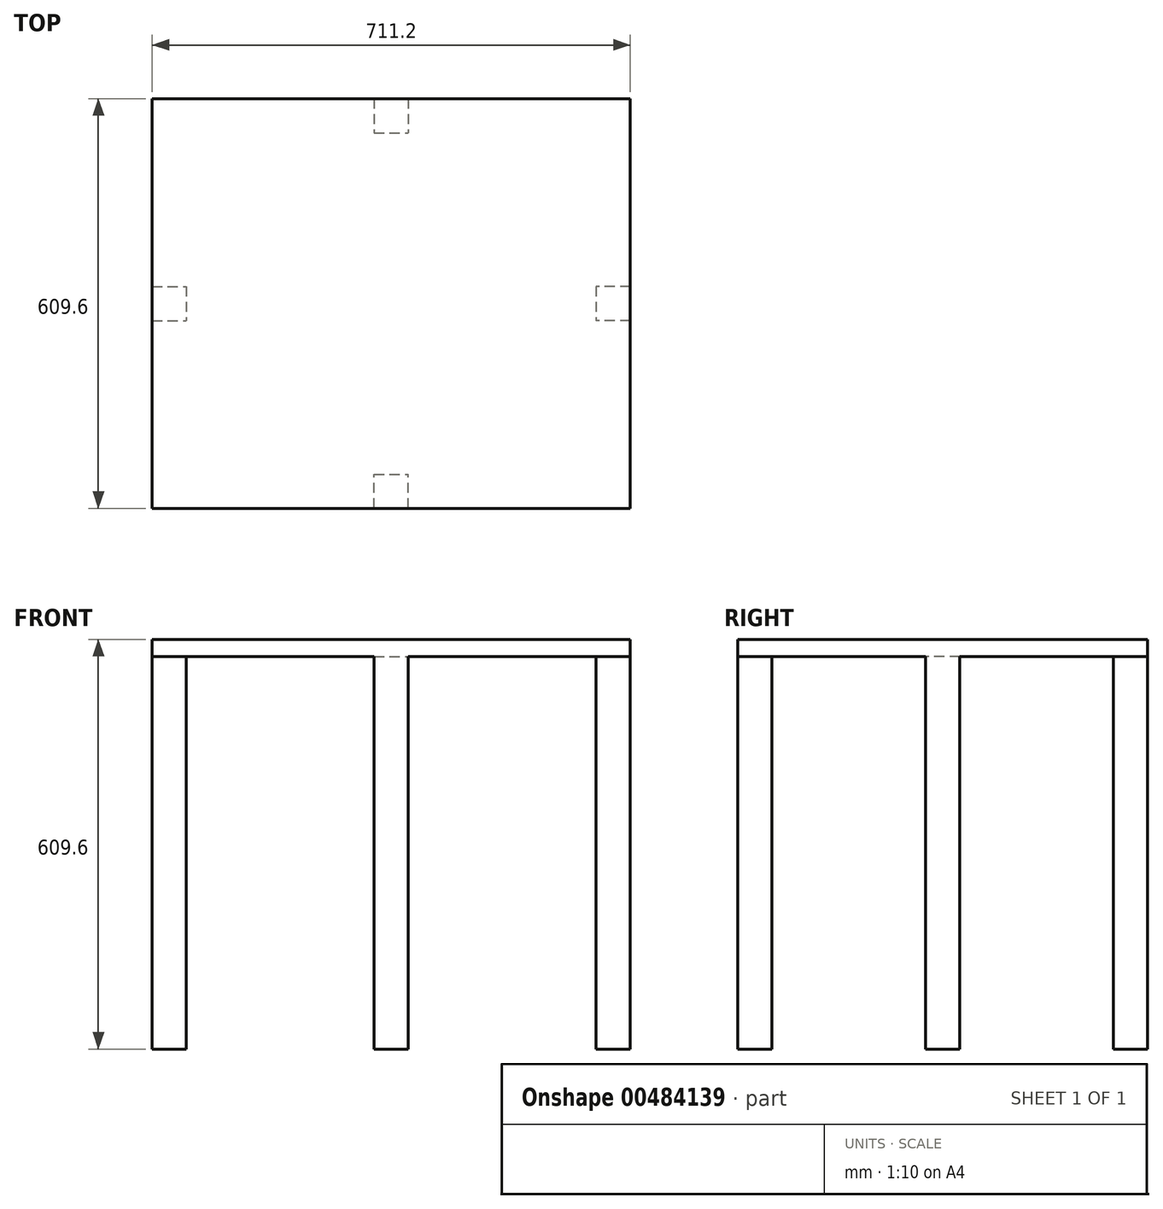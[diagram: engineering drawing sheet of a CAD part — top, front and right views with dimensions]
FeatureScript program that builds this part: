
annotation { "Feature Type Name" : "Feature", "Feature Type Description" : "" }
export const myFeature = defineFeature(function(context is Context, id is Id, definition is map)
    precondition{}
    {
        {
            var Q0;
            Q0=qCreatedBy(makeId("Top.planeOp"),FACE);
            var sketch = newSketch(context, id + "F0", { "sketchPlane" : qUnion([Q0])});
            skLineSegment(sketch, "E0.bottom", {"start": v(0, 0) * mm, "end": v(711.2, 0) * mm});
            skLineSegment(sketch, "E0.top", {"start": v(0, 609.6) * mm, "end": v(711.2, 609.6) * mm});
            skLineSegment(sketch, "E0.left", {"start": v(0, 0) * mm, "end": v(0, 609.6) * mm});
            skLineSegment(sketch, "E0.right", {"start": v(711.2, 0) * mm, "end": v(711.2, 609.6) * mm});
            skSolve(sketch);
        }
        {
            var Q0;
            Q0=qSketchRegion(id+"F0",true);
            extrude(context, id + "F1", {"entities" : qUnion([Q0]), "depth" : 25.4 * mm});
        }
        {
            var Q0;
            Q0=makeQuery(id+"F1.opExtrude","CAP_FACE",FACE,{"disambiguationData":[OSD([sQuery(id+"F0.wireOp",EDGE,"E0.bottom"),sQuery(id+"F0.wireOp",EDGE,"E0.top"),sQuery(id+"F0.wireOp",EDGE,"E0.left"),sQuery(id+"F0.wireOp",EDGE,"E0.right")])],"isStart":true});
            var sketch = newSketch(context, id + "F2", { "sketchPlane" : qUnion([Q0])});
            skLineSegment(sketch, "E1.top", {"start": v(0, -279.4) * mm, "end": v(50.8, -279.4) * mm});
            skLineSegment(sketch, "E1.left", {"start": v(0, -304.8) * mm, "end": v(0, -279.4) * mm});
            skLineSegment(sketch, "E1.right", {"start": v(50.8, -330.2) * mm, "end": v(50.8, -279.4) * mm});
            skLineSegment(sketch, "E2.top", {"start": v(0, -330.2) * mm, "end": v(50.8, -330.2) * mm});
            skLineSegment(sketch, "E2.left", {"start": v(0, -304.8) * mm, "end": v(0, -330.2) * mm});
            skLineSegment(sketch, "E3.MirrorCS", {"start": v(711.2, -508) * mm, "end": v(711.2, -279.4) * mm});
            skLineSegment(sketch, "E4.MirrorCS", {"start": v(711.2, -330.2) * mm, "end": v(711.2, -508) * mm});
            skLineSegment(sketch, "E5.MirrorCS", {"start": v(711.2, -330.2) * mm, "end": v(660.4, -330.2) * mm});
            skLineSegment(sketch, "E6.MirrorCS", {"start": v(660.4, -330.2) * mm, "end": v(660.4, -279.4) * mm});
            skLineSegment(sketch, "E7.MirrorCS", {"start": v(711.2, -279.4) * mm, "end": v(660.4, -279.4) * mm});
            skLineSegment(sketch, "E8.bottom", {"start": v(330.2, -609.6) * mm, "end": v(381, -609.6) * mm});
            skLineSegment(sketch, "E8.top", {"start": v(330.2, -558.8) * mm, "end": v(381, -558.8) * mm});
            skLineSegment(sketch, "E8.left", {"start": v(330.2, -609.6) * mm, "end": v(330.2, -558.8) * mm});
            skLineSegment(sketch, "E8.right", {"start": v(381, -609.6) * mm, "end": v(381, -558.8) * mm});
            skPoint(sketch, "E9.orphan", {"position": v(355.6, 0) * mm});
            skPoint(sketch, "E10.end.orphan", {"position": v(355.6, -609.6) * mm});
            skLineSegment(sketch, "E11.MirrorCS", {"start": v(330.2, 0) * mm, "end": v(381, 0) * mm});
            skLineSegment(sketch, "E12.MirrorCS", {"start": v(330.2, 0) * mm, "end": v(330.2, -50.8) * mm});
            skLineSegment(sketch, "E13.MirrorCS", {"start": v(330.2, -50.8) * mm, "end": v(381, -50.8) * mm});
            skLineSegment(sketch, "E14.MirrorCS", {"start": v(381, 0) * mm, "end": v(381, -50.8) * mm});
            skSolve(sketch);
        }
        {
            var Q0;
            Q0=qSketchRegion(id+"F2",true);
            extrude(context, id + "F3", {"entities" : qUnion([Q0]), "operationType" : NewBodyOperationType.ADD, "depth" : 584.2 * mm});
        }
    });
